# Revit family: CADS_Vent-Axia_Lo-CarbonSentinelMultivent
name_source: partatom
category: Mechanical Equipment
revit_build: Autodesk Revit 2015 (Build: 20160512_1515(x64)
units: mm (PartAtom-declared; Revit-internal decimal feet)

## types (4) — shared parameters
Apparent Load = 690 VA
AssetType = Fixed
Category = PR_65_67_29:Fans
Color = Dark Grey
Default Elevation = 1219 mm
DurationUnit = year
ExpectedLife = 20
IfcExportAs = IfcFanType
IfcExportType = USERDEFINED
Manufacturer = Vent-Axia Limited
Material = ABS Plastic
Name = MEV Unit
NominalHeight = 310 mm  [stored 1.01706 ft]
NominalLength = 340 mm  [stored 1.11549 ft]
NominalWidth = 260 mm  [stored 0.853018 ft]
NumberOfPoles = 1
RatedCurrent = 3 A
RatedVoltage = 230 V
Shape = Rectangular
Size = 260mm x 340mm x 310mm 
249mm x 340mm x 310mm
SpigotDiameter = 125 mm  [stored 0.410105 ft]
Version = 1.0
WarrantyDurationLabor = 2
WarrantyDurationMotors = 5
WarrantyDurationParts = 2
WarrantyDurationUnit = year

## per-type parameters (varying)
| type | Description | Features | ModelNumber |
| Sentinel Multivent | Lo-Carbon Sentinel Multivent |  | 437601 |
| Sentinel Multivent H | Lo-Carbon Sentinel Multivent H | Humidistat | 445655 |
| Sentinel Multivent Plus | Lo-Carbon Sentinel Multivent Plus |  | 407001 |
| Sentinel Multivent Plus H | Lo-Carbon Sentinel Multivent Plus H |  | 407849 |

note: column(s) folded — value = type name in every type: Model, ModelReference

note: [stored X ft] marks values corroborated as IEEE doubles in the binary element streams (Revit-internal decimal feet)

## geometry (parser evidence)
native form markers: Sweep x2
no freeform markers — native parametric forms only
